# Revit family: IS_Tempo_E1103_BIM_GB
name_source: partatom
category: Plumbing Fixtures
revit_build: Autodesk Revit MEP 2014 (Build: 20130308_1515(x64)
units: mm (PartAtom-declared; Revit-internal decimal feet)

## types (2) — shared parameters
Accessories = www.idealspec.co.uk
AreaUnits = millimeters
Assembly Code = C1030200
AssetType = Fixed
BREEAM = No
Brand = Ideal Standard
ConnectionType = Mechanical
Default Elevation = 800 mm  [stored 2.62467 ft]
Description = Tempo wall hung 500mm vanity unit with 2 drawers
DurationUnit = year
ECA = No
ExpectedLife = 30
Features = Wall hung 500mm vanity unit with 2 drawers
IfcExportAs = IfcFurnitureType
IfcExportType = CABINET
InstallationInstructions = www.idealspec.co.uk/resources.html
LinearUnits = millimeters
ManufacturerURL = www.idealspec.co.uk
MetalMtl = ISI_IdealStandard_Sanitaryware_Chrome_Render
ModelReference = Tempo wall hung 500mm vanity unit with 2 drawers
NBSDescription = Bathroom integrated duct work
NBSReference = 45-35-72/320
NettWeight = 15 Kg
NominalHeight = 550 mm
NominalLength = 440 mm  [stored 1.44357 ft]
NominalWidth = 500 mm
Shape = Rectangular
Size = 550 x 440 x 500 mm
Space = Internal
SpareParts = www.fastpart-spares.co.uk
SustainabilityPerformance = FSC
TMV3 = No
URL = www.idealspec.co.uk
Uniclass2015Description = Bathroom furniture
Uniclass2015Reference = Pr_40_30_78_05
Uniclass2015Version = Products v1.1
Version = 1
VolumeUnits = Litres
WRAS = No
WarrantyDescription = Manufacturers Warranty
WarrantyDurationParts = 25
WarrantyDurationUnit = year
WaterEfficientProduct = No
zero-valued in all types: Cost

## per-type parameters (varying)
| type | BIMObjectName | Color | Finish | LaminateMtl | Model | ModelNumber | Name | NominalDepth | ProductInformation |
| E1103SG - Tempo 500mm Vanity Unit - Wall Hung - 2 Drawers - SandyGrey | ISI_IdealStandard_Furniture_Tempo_E1103SG | Sandy grey | Sandy grey | ISI_IdealStandard_Sanitaryware_SandyGrey_SG_Render | E1103SG | E1103SG | Furniture_Tempo_E1103SG_IdealStandard | 0 mm  [stored 0 ft] | www.idealspec.co.uk/assets/datasheet/E1103SG |
| E1103WG - Tempo 500mm Vanity Unit - Wall Hung - 2 Drawers - White Gloss | ISI_IdealStandard_Furniture_Tempo_E1103WG | White gloss | White gloss | ISI_IdealStandard_Sanitaryware_WhiteGloss_WG_Render | E1103WG | E1103WG | Furniture_Tempo_E1103WG_IdealStandard | 440 mm  [stored 1.44357 ft] | www.idealspec.co.uk/assets/datasheet/E1103WG |

note: [stored X ft] marks values corroborated as IEEE doubles in the binary element streams (Revit-internal decimal feet)

## geometry (parser evidence)
native form markers: Sweep x3
no freeform markers — native parametric forms only
